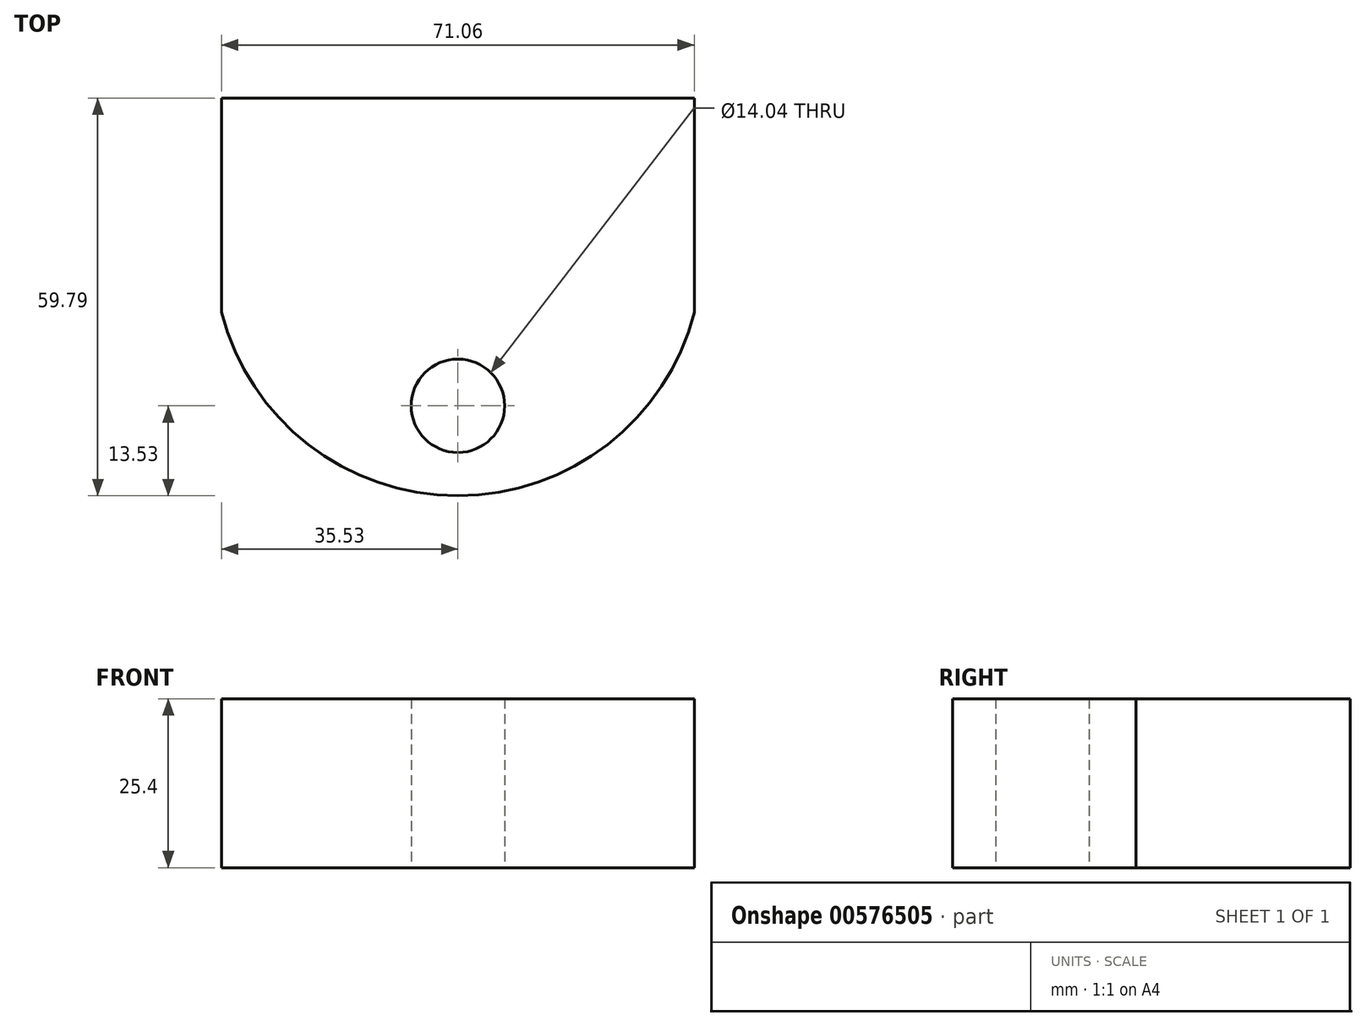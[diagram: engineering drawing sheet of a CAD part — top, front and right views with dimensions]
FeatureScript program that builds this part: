
annotation { "Feature Type Name" : "Feature", "Feature Type Description" : "" }
export const myFeature = defineFeature(function(context is Context, id is Id, definition is map)
    precondition{}
    {
        {
            var Q0;
            Q0=qCreatedBy(makeId("Top.planeOp"),FACE);
            var sketch = newSketch(context, id + "F0", { "sketchPlane" : qUnion([Q0])});
            skLineSegment(sketch, "E0.bottom", {"start": v(35.53, 16.1) * mm, "end": v(-35.53, 16.1) * mm});
            skLineSegment(sketch, "E0.top", {"start": v(35.53, -16.1) * mm, "end": v(-35.53, -16.1) * mm});
            skLineSegment(sketch, "E0.left", {"start": v(35.53, 16.1) * mm, "end": v(35.53, -16.1) * mm});
            skLineSegment(sketch, "E0.right", {"start": v(-35.53, 16.1) * mm, "end": v(-35.53, -16.1) * mm});
            skPoint(sketch, "E0.middle", {"position": v(0, 0) * mm});
            skArc(sketch, "E1", {"start": v(-35.53, -16.1) * mm, "mid": v(0, -43.7) * mm, "end": v(35.53, -16.1) * mm});
            skCircle(sketch, "E2", {"center": v(0, -30.17) * mm, "radius": 7.02 * mm});
            skPoint(sketch, "E2.centerSnap0", {"position": v(0, -16.1) * mm});
            skSolve(sketch);
        }
        {
            var Q0;
            Q0 = qSketchRegion(id + "F0", true);
            extrude(context, id + "F1", {"entities" : qUnion([Q0]), "depth" : 25.4 * mm, "offsetDistance" : 25.4 * mm});
        }
    });
